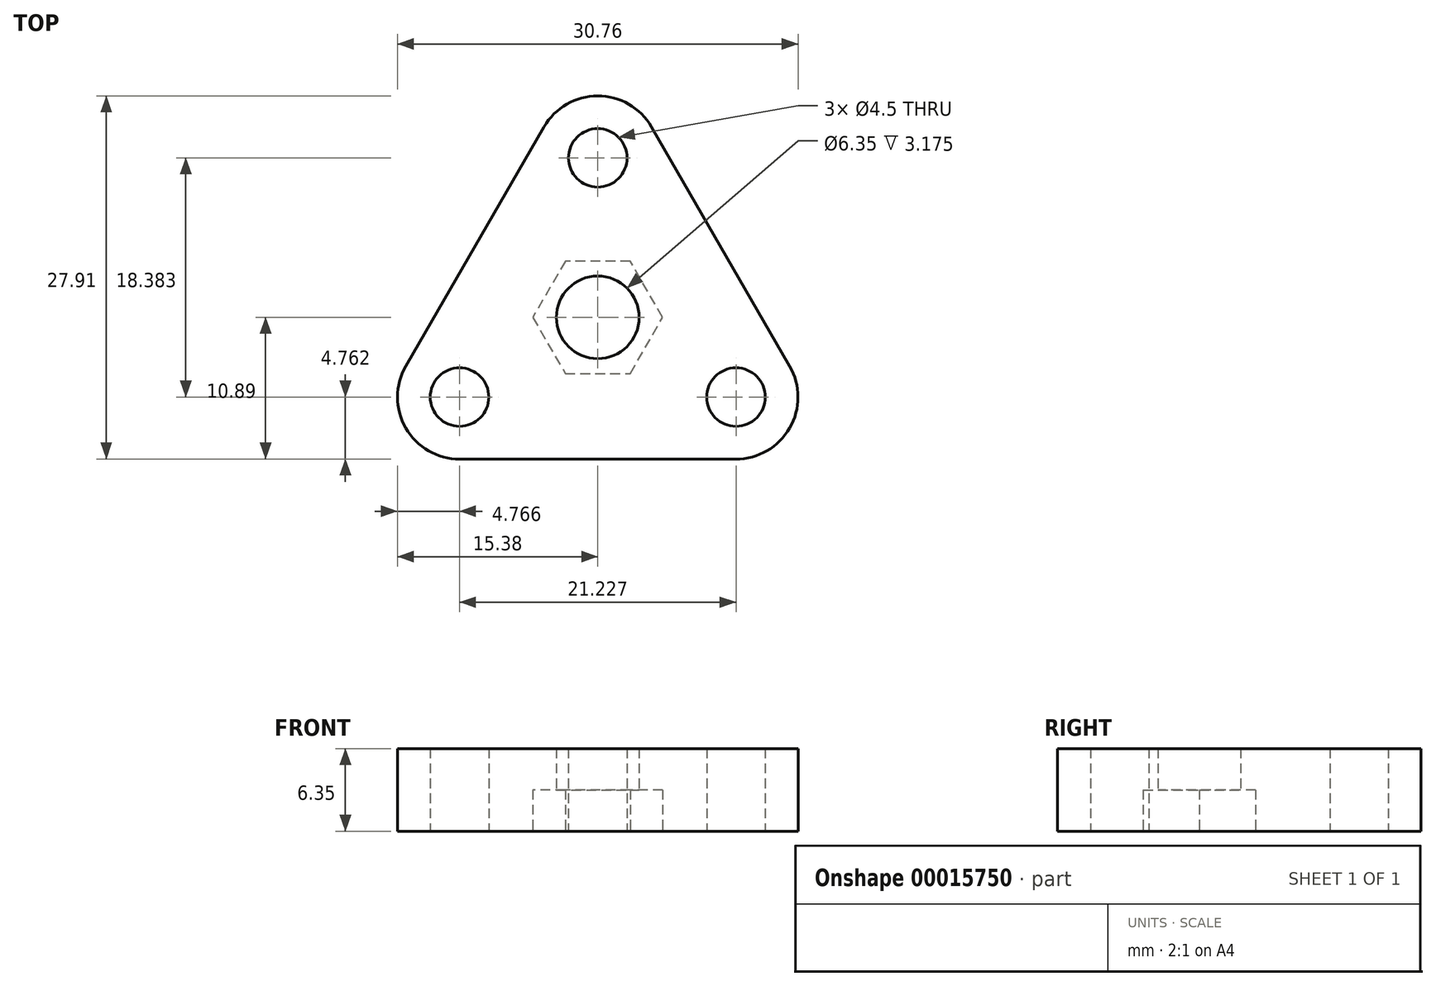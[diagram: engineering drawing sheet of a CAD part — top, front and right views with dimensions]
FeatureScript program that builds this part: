
annotation { "Feature Type Name" : "Feature", "Feature Type Description" : "" }
export const myFeature = defineFeature(function(context is Context, id is Id, definition is map)
    precondition{}
    {
        {
            var Q0;
            Q0=qCreatedBy(makeId("Top.planeOp"),FACE);
            var sketch = newSketch(context, id + "F0", { "sketchPlane" : qUnion([Q0])});
            skCircle(sketch, "E0", {"center": v(0, 0) * mm, "radius": 7.5 * mm, "construction": true});
            skCircle(sketch, "E1.cCircle", {"center": v(0, 0) * mm, "radius": 6.13 * mm, "construction": true});
            skLineSegment(sketch, "E1.0", {"start": v(10.61, -6.13) * mm, "end": v(-10.61, -6.13) * mm, "construction": true});
            skLineSegment(sketch, "E1.1", {"start": v(-10.61, -6.13) * mm, "end": v(0, 12.26) * mm, "construction": true});
            skLineSegment(sketch, "E1.2", {"start": v(0, 12.26) * mm, "end": v(10.61, -6.13) * mm, "construction": true});
            skPoint(sketch, "E1.0.midPoint", {"position": v(0, -6.13) * mm});
            skArc(sketch, "E2", {"start": v(-10.61, -10.9) * mm, "mid": v(-6.49, -3.75) * mm, "end": v(-14.74, -3.75) * mm, "construction": true});
            skArc(sketch, "E3", {"start": v(-14.74, -3.75) * mm, "mid": v(-14.74, -8.5) * mm, "end": v(-10.61, -10.9) * mm});
            skArc(sketch, "E4", {"start": v(4.12, 14.64) * mm, "mid": v(0, 17.02) * mm, "end": v(-4.12, 14.64) * mm});
            skArc(sketch, "E5", {"start": v(10.61, -10.9) * mm, "mid": v(14.74, -8.5) * mm, "end": v(14.74, -3.75) * mm});
            skLineSegment(sketch, "E6", {"start": v(-14.74, -3.75) * mm, "end": v(-4.12, 14.64) * mm});
            skLineSegment(sketch, "E7", {"start": v(4.12, 14.64) * mm, "end": v(14.74, -3.75) * mm});
            skLineSegment(sketch, "E8", {"start": v(10.61, -10.9) * mm, "end": v(-10.61, -10.9) * mm});
            skCircle(sketch, "E9", {"center": v(0, 0) * mm, "radius": 3.18 * mm});
            skCircle(sketch, "E10", {"center": v(0, 12.26) * mm, "radius": 2.25 * mm});
            skCircle(sketch, "E11", {"center": v(-10.61, -6.13) * mm, "radius": 2.25 * mm});
            skCircle(sketch, "E12", {"center": v(10.61, -6.13) * mm, "radius": 2.25 * mm});
            skSolve(sketch);
        }
        {
            var Q0;
            Q0 = qSketchRegion(id + "F0", true);
            extrude(context, id + "F1", {"entities" : qUnion([Q0]), "depth" : 6.35 * mm});
        }
        {
            var Q0;
            Q0=makeQuery(id+"F1.opExtrude","CAP_FACE",FACE,{"disambiguationData":[OSD([sQuery(id+"F0.wireOp",EDGE,"E3"),sQuery(id+"F0.wireOp",EDGE,"E4"),sQuery(id+"F0.wireOp",EDGE,"E5"),sQuery(id+"F0.wireOp",EDGE,"E6"),sQuery(id+"F0.wireOp",EDGE,"E7"),sQuery(id+"F0.wireOp",EDGE,"E8"),sQuery(id+"F0.wireOp",EDGE,"E9"),sQuery(id+"F0.wireOp",EDGE,"E10"),sQuery(id+"F0.wireOp",EDGE,"E11"),sQuery(id+"F0.wireOp",EDGE,"E12")])],"isStart":true});
            var sketch = newSketch(context, id + "F2", { "sketchPlane" : qUnion([Q0])});
            skCircle(sketch, "E13.cCircle", {"center": v(0, 0) * mm, "radius": 4.32 * mm, "construction": true});
            skLineSegment(sketch, "E13.0", {"start": v(-2.5, -4.32) * mm, "end": v(-4.99, 0) * mm});
            skLineSegment(sketch, "E13.1", {"start": v(-4.99, 0) * mm, "end": v(-2.5, 4.32) * mm});
            skLineSegment(sketch, "E13.2", {"start": v(-2.5, 4.32) * mm, "end": v(2.5, 4.32) * mm});
            skLineSegment(sketch, "E13.3", {"start": v(2.5, 4.32) * mm, "end": v(4.99, 0) * mm});
            skLineSegment(sketch, "E13.4", {"start": v(4.99, 0) * mm, "end": v(2.5, -4.32) * mm});
            skLineSegment(sketch, "E13.5", {"start": v(2.5, -4.32) * mm, "end": v(-2.5, -4.32) * mm});
            skPoint(sketch, "E13.0.midPoint", {"position": v(-3.74, -2.16) * mm});
            skSolve(sketch);
        }
        {
            var Q0;
            Q0 = qSketchRegion(id + "F2", true);
            extrude(context, id + "F3", {"entities" : qUnion([Q0]), "operationType" : NewBodyOperationType.REMOVE, "oppositeDirection" : true, "depth" : 3.17 * mm});
        }
    });
